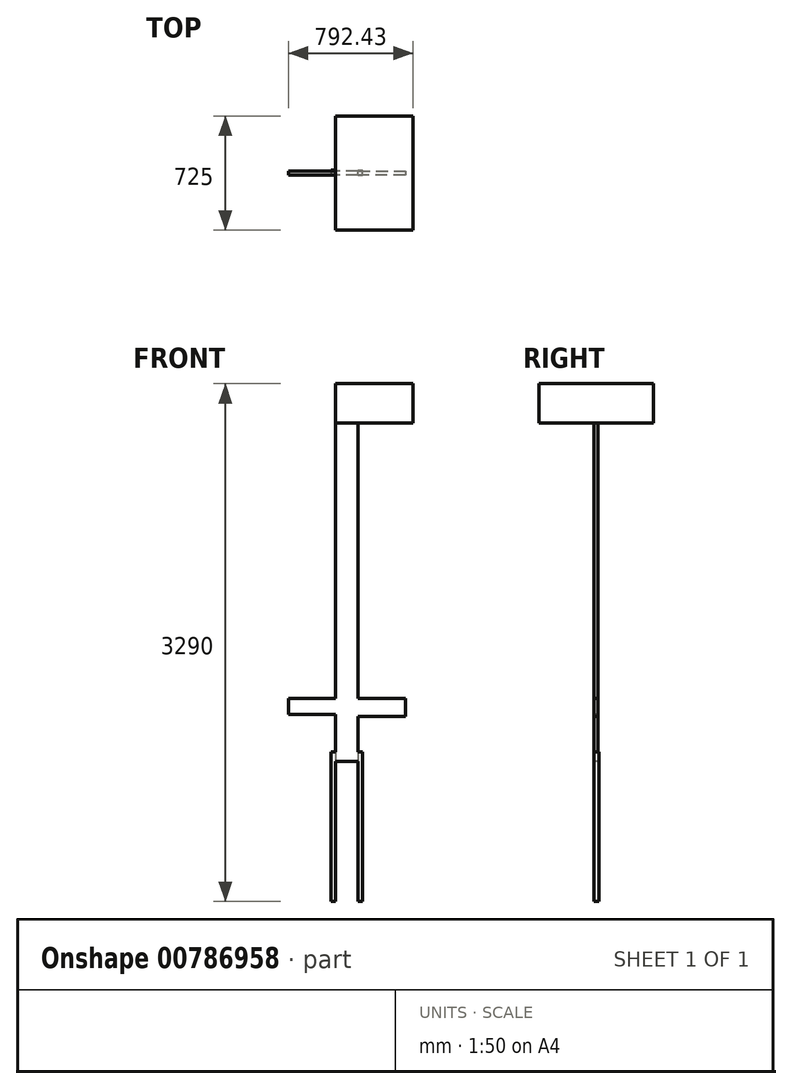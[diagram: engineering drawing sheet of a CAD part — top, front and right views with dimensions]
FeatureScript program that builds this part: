
annotation { "Feature Type Name" : "Feature", "Feature Type Description" : "" }
export const myFeature = defineFeature(function(context is Context, id is Id, definition is map)
    precondition{}
    {
        {
            var Q0;
            Q0=qCreatedBy(makeId("Top.planeOp"),FACE);
            var sketch = newSketch(context, id + "F0", { "sketchPlane" : qUnion([Q0])});
            skLineSegment(sketch, "E0.bottom", {"start": v(-1081.82, -150.3) * mm, "end": v(-1051.82, -150.3) * mm});
            skLineSegment(sketch, "E0.top", {"start": v(-1081.82, -180.3) * mm, "end": v(-1051.82, -180.3) * mm});
            skLineSegment(sketch, "E0.left", {"start": v(-1081.82, -150.3) * mm, "end": v(-1081.82, -180.3) * mm});
            skLineSegment(sketch, "E0.right", {"start": v(-1051.82, -150.3) * mm, "end": v(-1051.82, -180.3) * mm});
            skLineSegment(sketch, "E1.bottom", {"start": v(-909.39, -180.3) * mm, "end": v(-879.39, -180.3) * mm});
            skLineSegment(sketch, "E1.top", {"start": v(-909.39, -150.3) * mm, "end": v(-879.39, -150.3) * mm});
            skLineSegment(sketch, "E1.left", {"start": v(-909.39, -180.3) * mm, "end": v(-909.39, -150.3) * mm});
            skLineSegment(sketch, "E1.right", {"start": v(-879.39, -180.3) * mm, "end": v(-879.39, -150.3) * mm});
            skLineSegment(sketch, "E2", {"start": v(-1051.82, -165.3) * mm, "end": v(-1051.82, -160.3) * mm});
            skLineSegment(sketch, "E3", {"start": v(-1051.82, -160.3) * mm, "end": v(-1051.82, -170.3) * mm});
            skLineSegment(sketch, "E4", {"start": v(-1051.82, -170.3) * mm, "end": v(-909.39, -170.3) * mm});
            skLineSegment(sketch, "E5", {"start": v(-909.39, -170.3) * mm, "end": v(-909.39, -160.3) * mm});
            skLineSegment(sketch, "E6", {"start": v(-909.39, -160.3) * mm, "end": v(-1051.82, -160.3) * mm});
            skSolve(sketch);
        }
        {
            var Q0;
            {var subQ3=sQuery(id+"F0.wireOp",EDGE,"E1.bottom");Q0=makeQuery(id+"F0.imprint","IMPRINT",FACE,{"disambiguationData":[TD([[makeQuery(id+"F0.imprint","IMPRINT",EDGE,{"derivedFrom":subQ3}),1.0]])]});}
            var Q1;
            {var subQ1=sQuery(id+"F0.wireOp",EDGE,"E0.bottom");Q1=makeQuery(id+"F0.imprint","IMPRINT",FACE,{"disambiguationData":[TD([[makeQuery(id+"F0.imprint","IMPRINT",EDGE,{"derivedFrom":subQ1}),-1.0]])]});}
            extrude(context, id + "F1", {"entities" : qUnion([Q0, Q1]), "depth" : 950 * mm, "offsetDistance" : 25 * mm});
        }
        {
            var Q0;
            Q0=makeQuery(id+"F1.opExtrude","SWEPT_FACE",FACE,{"disambiguationData":[OSD([sQuery(id+"F0.wireOp",EDGE,"E0.top")])]});
            var sketch = newSketch(context, id + "F2", { "sketchPlane" : qUnion([Q0])});
            skLineSegment(sketch, "E7", {"start": v(-1081.82, 950) * mm, "end": v(-1081.82, 890) * mm});
            skLineSegment(sketch, "E8.0.0", {"start": v(-909.39, 0) * mm, "end": v(-879.39, 0) * mm});
            skLineSegment(sketch, "E8.0.1", {"start": v(-879.39, 0) * mm, "end": v(-879.39, 950) * mm});
            skLineSegment(sketch, "E8.0.2", {"start": v(-879.39, 950) * mm, "end": v(-909.39, 950) * mm});
            skLineSegment(sketch, "E8.0.3", {"start": v(-909.39, 950) * mm, "end": v(-909.39, 0) * mm});
            skLineSegment(sketch, "E9", {"start": v(-1081.82, 890) * mm, "end": v(-879.39, 890) * mm});
            skLineSegment(sketch, "E10", {"start": v(-879.39, 890) * mm, "end": v(-879.39, 950) * mm});
            skLineSegment(sketch, "E11", {"start": v(-1081.82, 950) * mm, "end": v(-879.39, 950) * mm});
            skSolve(sketch);
        }
        {
            var Q0;
            {var subQ0=sQuery(id+"F2.wireOp",EDGE,"E11");var subQ1=sQuery(id+"F2.wireOp",EDGE,"E8.0.3");var subQ2=makeQuery(id+"F2.imprint","INTERSECT",VERTEX,{"derivedFrom":[subQ1,subQ0]});Q0=makeQuery(id+"F2.imprint","IMPRINT",FACE,{"disambiguationData":[TD([[makeQuery(id+"F2.imprint","IMPRINT",EDGE,{"disambiguationData":[TD([[subQ2,-1.0]])],"derivedFrom":subQ1}),-1.0]])]});}
            extrude(context, id + "F3", {"entities" : qUnion([Q0]), "oppositeDirection" : true, "depth" : 25 * mm, "offsetDistance" : 25 * mm});
        }
        {
            var Q0;
            Q0=makeQuery(id+"F3.opExtrude","SWEPT_FACE",FACE,{"disambiguationData":[OSD([sQuery(id+"F2.wireOp",EDGE,"E11")])]});
            var sketch = newSketch(context, id + "F4", { "sketchPlane" : qUnion([Q0])});
            skLineSegment(sketch, "E12.bottom", {"start": v(-1051.82, -180.3) * mm, "end": v(-909.39, -180.3) * mm});
            skLineSegment(sketch, "E12.top", {"start": v(-1051.82, -155.3) * mm, "end": v(-909.39, -155.3) * mm});
            skLineSegment(sketch, "E12.left", {"start": v(-1051.82, -180.3) * mm, "end": v(-1051.82, -155.3) * mm});
            skLineSegment(sketch, "E12.right", {"start": v(-909.39, -180.3) * mm, "end": v(-909.39, -155.3) * mm});
            skSolve(sketch);
        }
        {
            var Q0;
            Q0 = qSketchRegion(id + "F4", true);
            extrude(context, id + "F5", {"entities" : qUnion([Q0]), "operationType" : NewBodyOperationType.ADD, "depth" : 340 * mm, "offsetDistance" : 25 * mm});
        }
        {
            var Q0;
            Q0=makeQuery(id+"F5.boolean.opBoolean","MERGE",FACE,{"derivedFrom":[makeQuery(id+"F3.opExtrude","SWEPT_FACE",FACE,{"disambiguationData":[OSD([sQuery(id+"F2.wireOp",EDGE,"E8.0.3")])]}),makeQuery(id+"F5.opExtrude","SWEPT_FACE",FACE,{"disambiguationData":[OSD([sQuery(id+"F4.wireOp",EDGE,"E12.right")])]})]});
            var sketch = newSketch(context, id + "F6", { "sketchPlane" : qUnion([Q0])});
            skLineSegment(sketch, "E13", {"start": v(-155.3, 1290) * mm, "end": v(-155.3, 1175) * mm});
            skLineSegment(sketch, "E14", {"start": v(-155.3, 1175) * mm, "end": v(-180.3, 1175) * mm});
            skLineSegment(sketch, "E15", {"start": v(-180.3, 1175) * mm, "end": v(-180.3, 1290) * mm});
            skLineSegment(sketch, "E16", {"start": v(-180.3, 1290) * mm, "end": v(-155.3, 1290) * mm});
            skLineSegment(sketch, "E17.0", {"start": v(-180.3, 1290) * mm, "end": v(-180.3, 890) * mm});
            skLineSegment(sketch, "E18.0.0", {"start": v(-180.3, 890) * mm, "end": v(-180.3, 1290) * mm});
            skLineSegment(sketch, "E18.0.2", {"start": v(-155.3, 1290) * mm, "end": v(-155.3, 890) * mm});
            skLineSegment(sketch, "E18.0.3", {"start": v(-155.3, 890) * mm, "end": v(-180.3, 890) * mm});
            skPoint(sketch, "E19.0", {"position": v(-180.3, 1290) * mm});
            skSolve(sketch);
        }
        {
            var Q0;
            {var subQ0=sQuery(id+"F6.wireOp",EDGE,"E14");Q0=makeQuery(id+"F6.imprint","IMPRINT",FACE,{"disambiguationData":[TD([[makeQuery(id+"F6.imprint","IMPRINT",EDGE,{"derivedFrom":subQ0}),-1.0]])]});}
            extrude(context, id + "F7", {"entities" : qUnion([Q0]), "operationType" : NewBodyOperationType.ADD, "depth" : 300 * mm, "offsetDistance" : 25 * mm});
        }
        {
            var Q0;
            Q0=makeQuery(id+"F5.boolean.opBoolean","MERGE",FACE,{"derivedFrom":[makeQuery(id+"F3.opExtrude","SWEPT_FACE",FACE,{"disambiguationData":[OSD([sQuery(id+"F0.wireOp",EDGE,"E0.top"),sQuery(id+"F0.wireOp",EDGE,"E0.right")])]}),makeQuery(id+"F5.opExtrude","SWEPT_FACE",FACE,{"disambiguationData":[OSD([sQuery(id+"F4.wireOp",EDGE,"E12.left")])]})]});
            var sketch = newSketch(context, id + "F8", { "sketchPlane" : qUnion([Q0])});
            skLineSegment(sketch, "E20", {"start": v(155.3, 1290) * mm, "end": v(155.3, 1190) * mm});
            skLineSegment(sketch, "E21", {"start": v(155.3, 1190) * mm, "end": v(180.3, 1190) * mm});
            skLineSegment(sketch, "E22", {"start": v(180.3, 1190) * mm, "end": v(180.3, 1290) * mm});
            skLineSegment(sketch, "E23", {"start": v(180.3, 1290) * mm, "end": v(155.3, 1290) * mm});
            skSolve(sketch);
        }
        {
            var Q0;
            Q0 = qSketchRegion(id + "F8", true);
            extrude(context, id + "F9", {"entities" : qUnion([Q0]), "operationType" : NewBodyOperationType.ADD, "depth" : 300 * mm, "offsetDistance" : 25 * mm});
        }
        {
            var Q0;
            Q0=makeQuery(id+"F9.boolean.opBoolean","MERGE",FACE,{"derivedFrom":[makeQuery(id+"F7.boolean.opBoolean","MERGE",FACE,{"derivedFrom":[makeQuery(id+"F5.opExtrude","CAP_FACE",FACE,{"disambiguationData":[OSD([sQuery(id+"F4.wireOp",EDGE,"E12.bottom"),sQuery(id+"F4.wireOp",EDGE,"E12.top"),sQuery(id+"F4.wireOp",EDGE,"E12.left"),sQuery(id+"F4.wireOp",EDGE,"E12.right")])],"isStart":false}),makeQuery(id+"F7.opExtrude","SWEPT_FACE",FACE,{"disambiguationData":[OSD([sQuery(id+"F6.wireOp",EDGE,"E16")])]})]}),makeQuery(id+"F9.opExtrude","SWEPT_FACE",FACE,{"disambiguationData":[OSD([sQuery(id+"F8.wireOp",EDGE,"E23")])]})]});
            var sketch = newSketch(context, id + "F10", { "sketchPlane" : qUnion([Q0])});
            skLineSegment(sketch, "E24.0.1", {"start": v(-909.39, -180.3) * mm, "end": v(-609.39, -180.3) * mm});
            skLineSegment(sketch, "E24.0.3", {"start": v(-609.39, -180.3) * mm, "end": v(-1351.82, -180.3) * mm});
            skLineSegment(sketch, "E24.0.5", {"start": v(-1351.82, -180.3) * mm, "end": v(-1051.82, -180.3) * mm});
            skLineSegment(sketch, "E24.0.7", {"start": v(-1051.82, -180.3) * mm, "end": v(-909.39, -180.3) * mm});
            skLineSegment(sketch, "E25", {"start": v(-1051.82, -180.3) * mm, "end": v(-1051.82, -155.3) * mm});
            skLineSegment(sketch, "E26", {"start": v(-1051.82, -155.3) * mm, "end": v(-909.39, -180.3) * mm});
            skLineSegment(sketch, "E27", {"start": v(-909.39, -180.3) * mm, "end": v(-909.39, -155.3) * mm});
            skLineSegment(sketch, "E28", {"start": v(-909.39, -155.3) * mm, "end": v(-1051.82, -155.3) * mm});
            skSolve(sketch);
        }
        {
            var Q0;
            Q0 = qSketchRegion(id + "F10", true);
            extrude(context, id + "F11", {"entities" : qUnion([Q0]), "operationType" : NewBodyOperationType.ADD, "depth" : 2000 * mm, "offsetDistance" : 25 * mm});
        }
        {
            var Q0;
            Q0=makeQuery(id+"F11.boolean.opBoolean","MERGE",FACE,{"derivedFrom":[makeQuery(id+"F9.boolean.opBoolean","MERGE",FACE,{"derivedFrom":[makeQuery(id+"F7.boolean.opBoolean","MERGE",FACE,{"derivedFrom":[makeQuery(id+"F5.boolean.opBoolean","MERGE",FACE,{"derivedFrom":[makeQuery(id+"F3.opExtrude","CAP_FACE",FACE,{"disambiguationData":[OSD([sQuery(id+"F0.wireOp",EDGE,"E0.top"),sQuery(id+"F0.wireOp",EDGE,"E0.right"),sQuery(id+"F2.wireOp",EDGE,"E8.0.3"),sQuery(id+"F2.wireOp",EDGE,"E9"),sQuery(id+"F2.wireOp",EDGE,"E11")])],"isStart":true}),makeQuery(id+"F5.opExtrude","SWEPT_FACE",FACE,{"disambiguationData":[OSD([sQuery(id+"F4.wireOp",EDGE,"E12.bottom")])]})]}),makeQuery(id+"F7.opExtrude","SWEPT_FACE",FACE,{"disambiguationData":[OSD([sQuery(id+"F6.wireOp",EDGE,"E17.0")])]})]}),makeQuery(id+"F9.opExtrude","SWEPT_FACE",FACE,{"disambiguationData":[OSD([sQuery(id+"F8.wireOp",EDGE,"E22")])]})]}),makeQuery(id+"F11.opExtrude","SWEPT_FACE",FACE,{"disambiguationData":[OSD([sQuery(id+"F10.wireOp",EDGE,"E24.0.7")])]})]});
            var sketch = newSketch(context, id + "F12", { "sketchPlane" : qUnion([Q0])});
            skLineSegment(sketch, "E29", {"start": v(-909.39, 3290) * mm, "end": v(-909.39, 3040) * mm});
            skLineSegment(sketch, "E30", {"start": v(-909.39, 3040) * mm, "end": v(-1051.82, 3040) * mm});
            skLineSegment(sketch, "E31", {"start": v(-1051.82, 3040) * mm, "end": v(-1051.82, 3290) * mm});
            skLineSegment(sketch, "E32", {"start": v(-1051.82, 3290) * mm, "end": v(-909.39, 3290) * mm});
            skSolve(sketch);
        }
        {
            var Q0;
            Q0 = qSketchRegion(id + "F12", true);
            extrude(context, id + "F13", {"entities" : qUnion([Q0]), "operationType" : NewBodyOperationType.ADD, "depth" : 350 * mm, "offsetDistance" : 25 * mm});
        }
        {
            var Q0;
            Q0=makeQuery(id+"F13.boolean.opBoolean","MERGE",FACE,{"derivedFrom":[makeQuery(id+"F11.opExtrude","SWEPT_FACE",FACE,{"disambiguationData":[OSD([sQuery(id+"F10.wireOp",EDGE,"E27")])]}),makeQuery(id+"F13.opExtrude","SWEPT_FACE",FACE,{"disambiguationData":[OSD([sQuery(id+"F12.wireOp",EDGE,"E29")])]})]});
            var sketch = newSketch(context, id + "F14", { "sketchPlane" : qUnion([Q0])});
            skLineSegment(sketch, "E33", {"start": v(-180.3, 3040) * mm, "end": v(-155.3, 3040) * mm});
            skSolve(sketch);
        }
        {
            var Q0;
            Q0 = qSketchRegion(id + "F14", true);
            var Q1;
            {var subQ3=sQuery(id+"F14.wireOp",EDGE,"E33");Q1=makeQuery(id+"F14.imprint","IMPRINT",FACE,{"disambiguationData":[TD([[makeQuery(id+"F14.imprint","IMPRINT",EDGE,{"derivedFrom":subQ3}),1.0]])]});}
            extrude(context, id + "F15", {"entities" : qUnion([Q0, Q1]), "operationType" : NewBodyOperationType.ADD, "depth" : 350 * mm, "offsetDistance" : 25 * mm});
        }
        {
            var Q0;
            {var subQ0=sQuery(id+"F10.wireOp",EDGE,"E28");var subQ1=sQuery(id+"F8.wireOp",EDGE,"E20");var subQ2=sQuery(id+"F6.wireOp",EDGE,"E18.0.2");var subQ3=sQuery(id+"F4.wireOp",EDGE,"E12.top");Q0=makeQuery(id+"F15.boolean.opBoolean","MERGE",FACE,{"derivedFrom":[makeQuery(id+"F11.boolean.opBoolean","MERGE",FACE,{"derivedFrom":[makeQuery(id+"F9.boolean.opBoolean","MERGE",FACE,{"derivedFrom":[makeQuery(id+"F7.boolean.opBoolean","MERGE",FACE,{"derivedFrom":[makeQuery(id+"F5.boolean.opBoolean","MERGE",FACE,{"derivedFrom":[makeQuery(id+"F3.opExtrude","CAP_FACE",FACE,{"disambiguationData":[OSD([sQuery(id+"F0.wireOp",EDGE,"E0.top"),sQuery(id+"F0.wireOp",EDGE,"E0.right"),sQuery(id+"F2.wireOp",EDGE,"E8.0.3"),sQuery(id+"F2.wireOp",EDGE,"E9"),sQuery(id+"F2.wireOp",EDGE,"E11")])],"isStart":false}),makeQuery(id+"F5.opExtrude","SWEPT_FACE",FACE,{"disambiguationData":[OSD([subQ3])]})]}),makeQuery(id+"F7.opExtrude","SWEPT_FACE",FACE,{"disambiguationData":[OSD([subQ2])]})]}),makeQuery(id+"F9.opExtrude","SWEPT_FACE",FACE,{"disambiguationData":[OSD([subQ1])]})]}),makeQuery(id+"F11.opExtrude","SWEPT_FACE",FACE,{"disambiguationData":[OSD([subQ0])]})]}),makeQuery(id+"F15.opExtrude","SWEPT_FACE",FACE,{"disambiguationData":[OSD([subQ3,sQuery(id+"F6.wireOp",EDGE,"E16"),subQ2,subQ1,sQuery(id+"F8.wireOp",EDGE,"E23"),sQuery(id+"F10.wireOp",EDGE,"E27"),subQ0])]})]});}
            var sketch = newSketch(context, id + "F16", { "sketchPlane" : qUnion([Q0])});
            skLineSegment(sketch, "E34", {"start": v(909.39, 3040) * mm, "end": v(1051.82, 3040) * mm});
            skSolve(sketch);
        }
        {
            var Q0;
            Q0 = qSketchRegion(id + "F16", true);
            var Q1;
            {var subQ8=sQuery(id+"F16.wireOp",EDGE,"E34");Q1=makeQuery(id+"F16.imprint","IMPRINT",FACE,{"disambiguationData":[TD([[makeQuery(id+"F16.imprint","IMPRINT",EDGE,{"derivedFrom":subQ8}),1.0]])]});}
            extrude(context, id + "F17", {"entities" : qUnion([Q0, Q1]), "operationType" : NewBodyOperationType.ADD, "depth" : 350 * mm, "offsetDistance" : 25 * mm});
        }
    });
